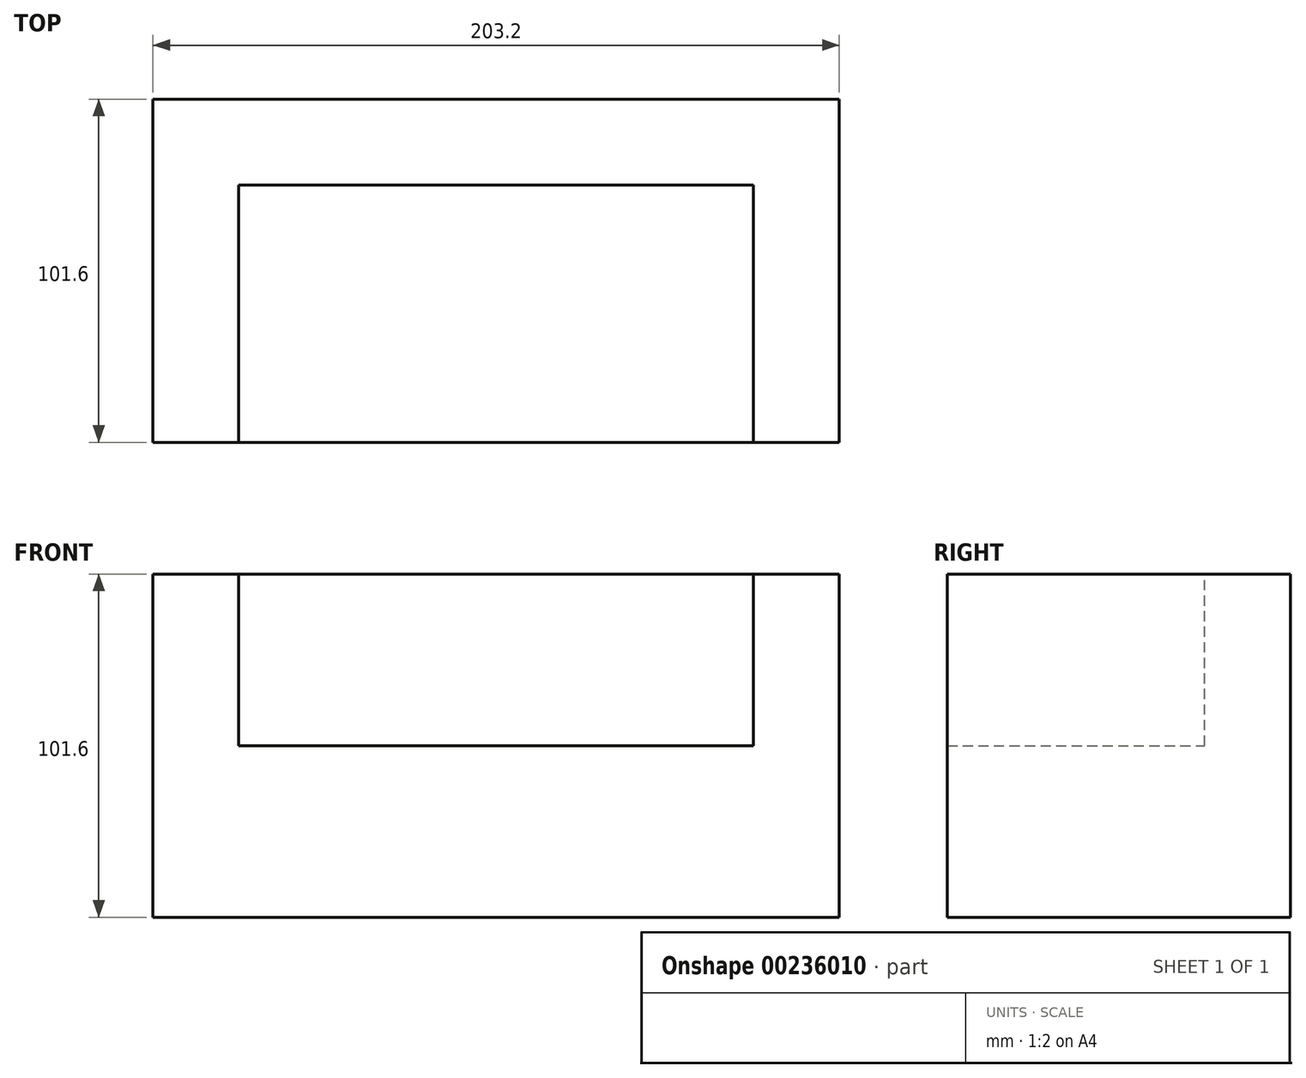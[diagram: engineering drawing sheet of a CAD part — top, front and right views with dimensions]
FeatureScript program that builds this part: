
annotation { "Feature Type Name" : "Feature", "Feature Type Description" : "" }
export const myFeature = defineFeature(function(context is Context, id is Id, definition is map)
    precondition{}
    {
        {
            var Q0;
            Q0=qCreatedBy(makeId("Top.planeOp"),FACE);
            var sketch = newSketch(context, id + "F0", { "sketchPlane" : qUnion([Q0])});
            skLineSegment(sketch, "E0.bottom", {"start": v(-142.53, -16.47) * mm, "end": v(60.67, -16.47) * mm});
            skLineSegment(sketch, "E0.top", {"start": v(-142.53, 85.13) * mm, "end": v(60.67, 85.13) * mm});
            skLineSegment(sketch, "E0.left", {"start": v(-142.53, -16.47) * mm, "end": v(-142.53, 85.13) * mm});
            skLineSegment(sketch, "E0.right", {"start": v(60.67, -16.47) * mm, "end": v(60.67, 85.13) * mm});
            skSolve(sketch);
        }
        {
            var Q0;
            Q0=makeQuery(id+"F0.imprint","IMPRINT",FACE,{"disambiguationData":[TD([[makeQuery(id+"F0.imprint","IMPRINT",EDGE,{"derivedFrom":sQuery(id+"F0.wireOp",EDGE,"E0.bottom")}),1.0]])]});
            extrude(context, id + "F1", {"entities" : qUnion([Q0]), "depth" : 101.6 * mm});
        }
        {
            var Q0;
            Q0=makeQuery(id+"F1.opExtrude","CAP_FACE",FACE,{"disambiguationData":[OSD([sQuery(id+"F0.wireOp",EDGE,"E0.bottom"),sQuery(id+"F0.wireOp",EDGE,"E0.top"),sQuery(id+"F0.wireOp",EDGE,"E0.left"),sQuery(id+"F0.wireOp",EDGE,"E0.right")])],"isStart":false});
            var sketch = newSketch(context, id + "F2", { "sketchPlane" : qUnion([Q0])});
            skLineSegment(sketch, "E1", {"start": v(-142.53, -16.47) * mm, "end": v(-117.13, -16.47) * mm});
            skLineSegment(sketch, "E2", {"start": v(60.67, -16.47) * mm, "end": v(35.27, -16.47) * mm});
            skLineSegment(sketch, "E3", {"start": v(35.27, -16.47) * mm, "end": v(35.27, 59.73) * mm});
            skLineSegment(sketch, "E4", {"start": v(-117.13, -16.47) * mm, "end": v(-117.13, 59.73) * mm});
            skLineSegment(sketch, "E5", {"start": v(-117.13, 59.73) * mm, "end": v(35.27, 59.73) * mm});
            skSolve(sketch);
        }
        {
            var Q0;
            {var subQ0=sQuery(id+"F2.wireOp",EDGE,"E3");Q0=makeQuery(id+"F2.imprint","IMPRINT",FACE,{"disambiguationData":[TD([[makeQuery(id+"F2.imprint","IMPRINT",EDGE,{"derivedFrom":subQ0}),1.0]])]});}
            extrude(context, id + "F3", {"entities" : qUnion([Q0]), "operationType" : NewBodyOperationType.REMOVE, "oppositeDirection" : true, "depth" : 76.2 * mm});
        }
        {
            var Q0;
            Q0=makeQuery(id+"F3.boolean.opBoolean","COPY",FACE,{"derivedFrom":makeQuery(id+"F3.opExtrude","CAP_FACE",FACE,{"disambiguationData":[OSD([sQuery(id+"F0.wireOp",EDGE,"E0.bottom"),sQuery(id+"F2.wireOp",EDGE,"E3"),sQuery(id+"F2.wireOp",EDGE,"E4"),sQuery(id+"F2.wireOp",EDGE,"E5")])],"isStart":false})});
            extrude(context, id + "F4", {"entities" : qUnion([Q0]), "operationType" : NewBodyOperationType.ADD, "depth" : 25.4 * mm});
        }
    });
